# Revit family: FAP33T-W
name_source: partatom
category: Communication Devices
revit_build: Autodesk Revit 2014 (Build: 20140709_2115(x64)
units: mm (PartAtom-declared; Revit-internal decimal feet)

## types (1)
- Two Way, Full Range, Coaxial Ceiling Loudspeaker
    100V Taps = 16W, 8W, 4W & 6Ω
    70V Taps = 16, 8, 4, 2 Watts & 6Ω
    Baffle Material = <By Category>
    Body Material = QF_Wall Paint-Gray
    Color = <By Category>
    Communication Ports = 4-Position PHX Type Connector
    Controls = Front Mounted Tap Selector Switch
    Cost = 101.99 $
    Cost MSRP = 101.99 $
    Coverage Horizontal = 110.00°
    Coverage Vertical = 0.00°
    Depth = 8.78 "
    Description = 3" FULL RANGE IN-CEILING LOUDSPEAKER WITH 16-WATT 70V/100V TRANSFORMER, PORTED ENCLOSURE, AND SAFETY FIRST MOUNTING SYSTEM
    Dispersion Angle = 57.00°
    Enclosure Material = <By Category>
    Environmental Testing = Humidity: MIL-STD-810G / High and Low Temperature: -20° and 70° C
    Family Code (default) = LOUD SPEAKERS
    Frequency Response  = 85Hz - 12kHz
    Grill Material = QF_Wall Paint-Gray
    Height = 5.39 "
    IQ Category = SPEAKERS
    Impedance = 6
    Ingress Protection = IP-21
    Input Connectors = 4-Position PHX Type Connector
    Manufacturer = ATLAS SOUND
    Manufacturer URL = https://www.atlasied.com
    Market = Commercial, Higher Education, Emergency
    MasterFormat = 27 41 13
    MaterFormat Title = SPEAKERS
    Max Input Ratings (8Ω) = 25W Continuous, 50W Program 12.5 Volts RMS, 21.2 Volts Peak
    Model = FAP33T-W
    Mount Material = QF_Plastic-White-Smooth
    Mounting/Rigging Provisions = Patented Safety First Mounting System
    OmniClass Number = 23-37 17 13 19
    OmniClass Title = SPEAKERS
    Operation Mode = Non-Powered Passive
    Power Rating (RMS) = 103 dB SPL / 108 dB SPL (peak 8Ω)
    Product Documentation Link = https://www.atlasied.com
    Product Page URL = https://www.atlasied.com
    Regulatory Compliance = UL Listed to Comply with UL1480, UL2043 and CSA60065. Suitable for Use in Air Handling Spaces per NFPA 70 and NFPA 90
    SPL Max = 104
    Safety Agency Ratings = UL Listed to Comply with UL1480, UL2043 and CSA60065. Suitable for Use in Air Handling Spaces per NFPA 70 and NFPA 90.
    Safety Features = 1 Safety Hang Point
    ScheduleType |RF| = AtlasIED Master
    Sensitivity = 104
    Speaker Dispersion = 135.00°
    Speaker Type = S1
    Transformer Option = Yes
    URL = www.atlassound.com
    Vertical Symmetry = Yes
    Warranty = 5 Year
    Weight Product = 4.14
    Width = 8.78 "

## geometry (parser evidence)
native form markers: Sweep x2
no freeform markers — native parametric forms only
